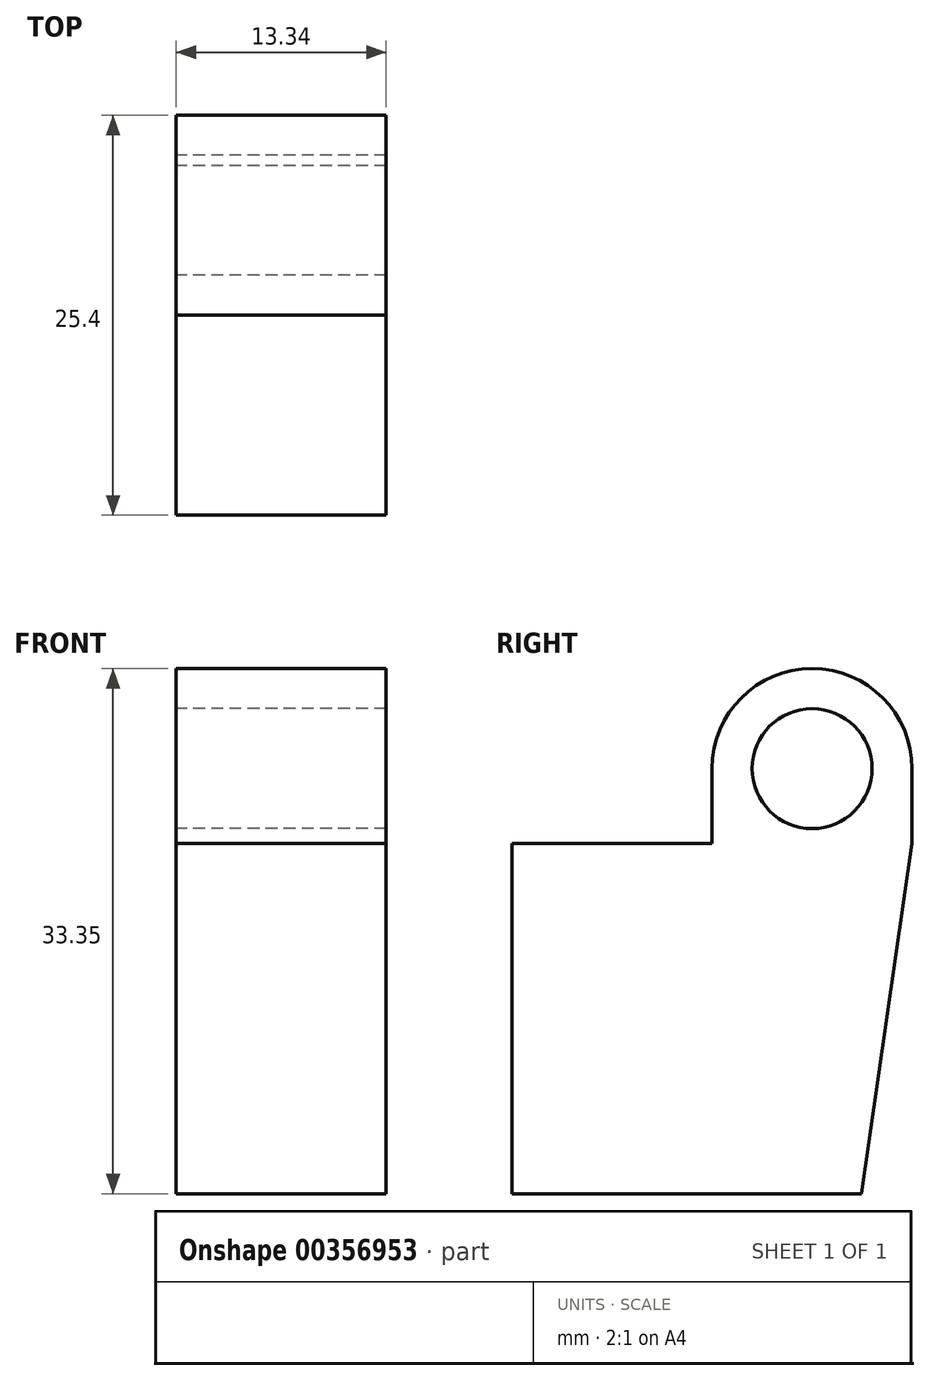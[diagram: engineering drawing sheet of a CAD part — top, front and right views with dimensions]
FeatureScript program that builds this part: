
annotation { "Feature Type Name" : "Feature", "Feature Type Description" : "" }
export const myFeature = defineFeature(function(context is Context, id is Id, definition is map)
    precondition{}
    {
        {
            var Q0;
            Q0=qCreatedBy(makeId("Front.planeOp"),FACE);
            var sketch = newSketch(context, id + "F0", { "sketchPlane" : qUnion([Q0])});
            skLineSegment(sketch, "E0.bottom", {"start": v(0, 0) * mm, "end": v(13.34, 0) * mm});
            skLineSegment(sketch, "E0.top", {"start": v(0, 22.25) * mm, "end": v(13.34, 22.25) * mm});
            skLineSegment(sketch, "E0.left", {"start": v(0, 0) * mm, "end": v(0, 22.25) * mm});
            skLineSegment(sketch, "E0.right", {"start": v(13.34, 0) * mm, "end": v(13.34, 22.25) * mm});
            skSolve(sketch);
        }
        {
            var Q0;
            Q0 = qSketchRegion(id + "F0", true);
            extrude(context, id + "F1", {"entities" : qUnion([Q0]), "depth" : 12.7 * mm});
        }
        {
            var Q0;
            Q0=qCreatedBy(makeId("Right.planeOp"),FACE);
            var sketch = newSketch(context, id + "F2", { "sketchPlane" : qUnion([Q0])});
            skLineSegment(sketch, "E1", {"start": v(0, 0) * mm, "end": v(0, 27) * mm});
            skLineSegment(sketch, "E2.left", {"start": v(0, 27) * mm, "end": v(0, 0) * mm});
            skLineSegment(sketch, "E2.right", {"start": v(12.7, 27) * mm, "end": v(12.7, 22.25) * mm});
            skCircle(sketch, "E3", {"center": v(6.35, 27) * mm, "radius": 3.81 * mm});
            skLineSegment(sketch, "E4", {"start": v(9.5, 0) * mm, "end": v(12.7, 22.25) * mm});
            skArc(sketch, "E5", {"start": v(12.7, 27) * mm, "mid": v(6.35, 33.35) * mm, "end": v(0, 27) * mm});
            skPoint(sketch, "E6.orphan", {"position": v(0, 31.75) * mm});
            skPoint(sketch, "E7.endSnap0", {"position": v(6.35, 33.35) * mm});
            skPoint(sketch, "E7.start.orphan", {"position": v(6.35, 33.35) * mm});
            skLineSegment(sketch, "E8", {"start": v(12.7, 22.25) * mm, "end": v(0, 22.25) * mm});
            skLineSegment(sketch, "E9", {"start": v(0, 0) * mm, "end": v(9.53, 0) * mm});
            skPoint(sketch, "E9.endSnap0", {"position": v(9.53, 0.23) * mm});
            skSolve(sketch);
        }
        {
            var Q0;
            Q0 = qSketchRegion(id + "F2", true);
            extrude(context, id + "F3", {"entities" : qUnion([Q0]), "operationType" : NewBodyOperationType.ADD, "depth" : 13.33 * mm});
        }
    });
